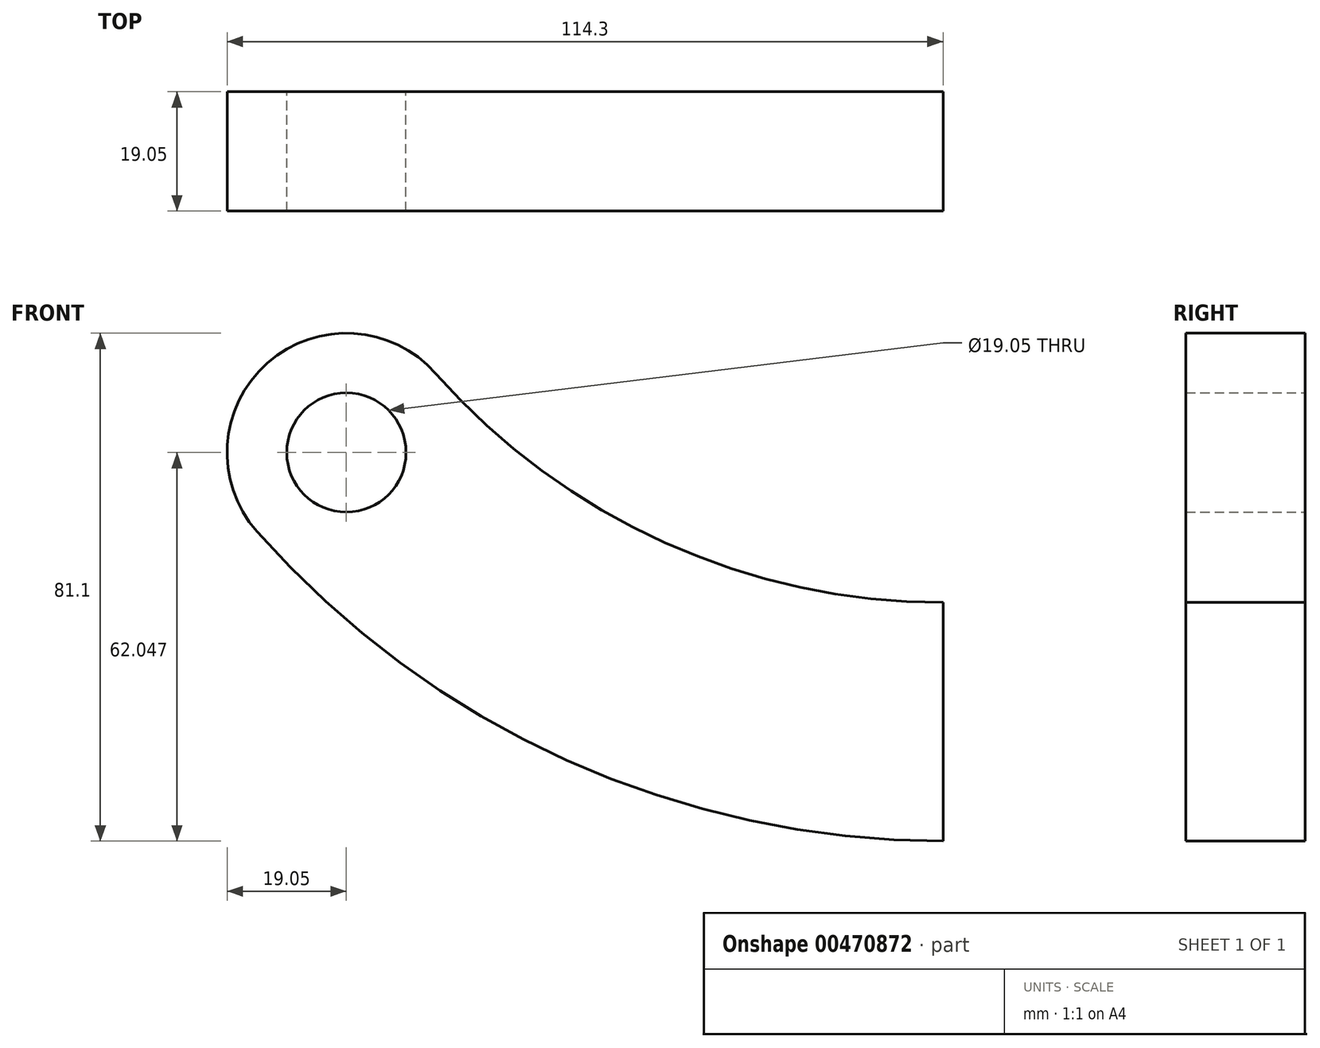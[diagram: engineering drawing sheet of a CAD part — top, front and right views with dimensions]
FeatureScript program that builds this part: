
annotation { "Feature Type Name" : "Feature", "Feature Type Description" : "" }
export const myFeature = defineFeature(function(context is Context, id is Id, definition is map)
    precondition{}
    {
        {
            var Q0;
            Q0=qCreatedBy(makeId("Front.planeOp"),FACE);
            var sketch = newSketch(context, id + "F0", { "sketchPlane" : qUnion([Q0])});
            skLineSegment(sketch, "E0", {"start": v(0, 0) * mm, "end": v(-95.25, 0) * mm});
            skLineSegment(sketch, "E1", {"start": v(0, 0) * mm, "end": v(0, 177.8) * mm});
            skLineSegment(sketch, "E2", {"start": v(-95.25, 0) * mm, "end": v(-95.25, 93.8) * mm});
            skArc(sketch, "E3.0", {"start": v(-109.54, 81.2) * mm, "mid": v(0, 31.75) * mm, "end": v(109.54, 81.2) * mm});
            skArc(sketch, "E4.0", {"start": v(-80.96, 106.4) * mm, "mid": v(0, 69.85) * mm, "end": v(80.96, 106.4) * mm});
            skCircle(sketch, "E5", {"center": v(-95.25, 93.8) * mm, "radius": 9.53 * mm});
            skArc(sketch, "E6", {"start": v(-80.96, 106.4) * mm, "mid": v(-107.85, 108.08) * mm, "end": v(-109.54, 81.2) * mm});
            skArc(sketch, "E7.MirrorCS", {"start": v(80.96, 106.4) * mm, "mid": v(107.85, 108.08) * mm, "end": v(109.54, 81.2) * mm});
            skCircle(sketch, "E8.MirrorC", {"center": v(95.25, 93.8) * mm, "radius": 9.53 * mm});
            skSolve(sketch);
        }
        {
            var Q0;
            Q0=makeQuery(id+"F0.imprint","IMPRINT",FACE,{"disambiguationData":[TD([[makeQuery(id+"F0.imprint","IMPRINT",EDGE,{"derivedFrom":sQuery(id+"F0.wireOp",EDGE,"E5")}),-1.0]])]});
            var Q1;
            {var subQ0=sQuery(id+"F0.wireOp",EDGE,"E7.MirrorCS");Q1=makeQuery(id+"F0.imprint","IMPRINT",FACE,{"disambiguationData":[TD([[makeQuery(id+"F0.imprint","IMPRINT",EDGE,{"derivedFrom":subQ0}),-1.0]])]});}
            extrude(context, id + "F1", {"entities" : qUnion([Q0, Q1]), "depth" : 19.05 * mm, "offsetDistance" : 25.4 * mm});
        }
    });
